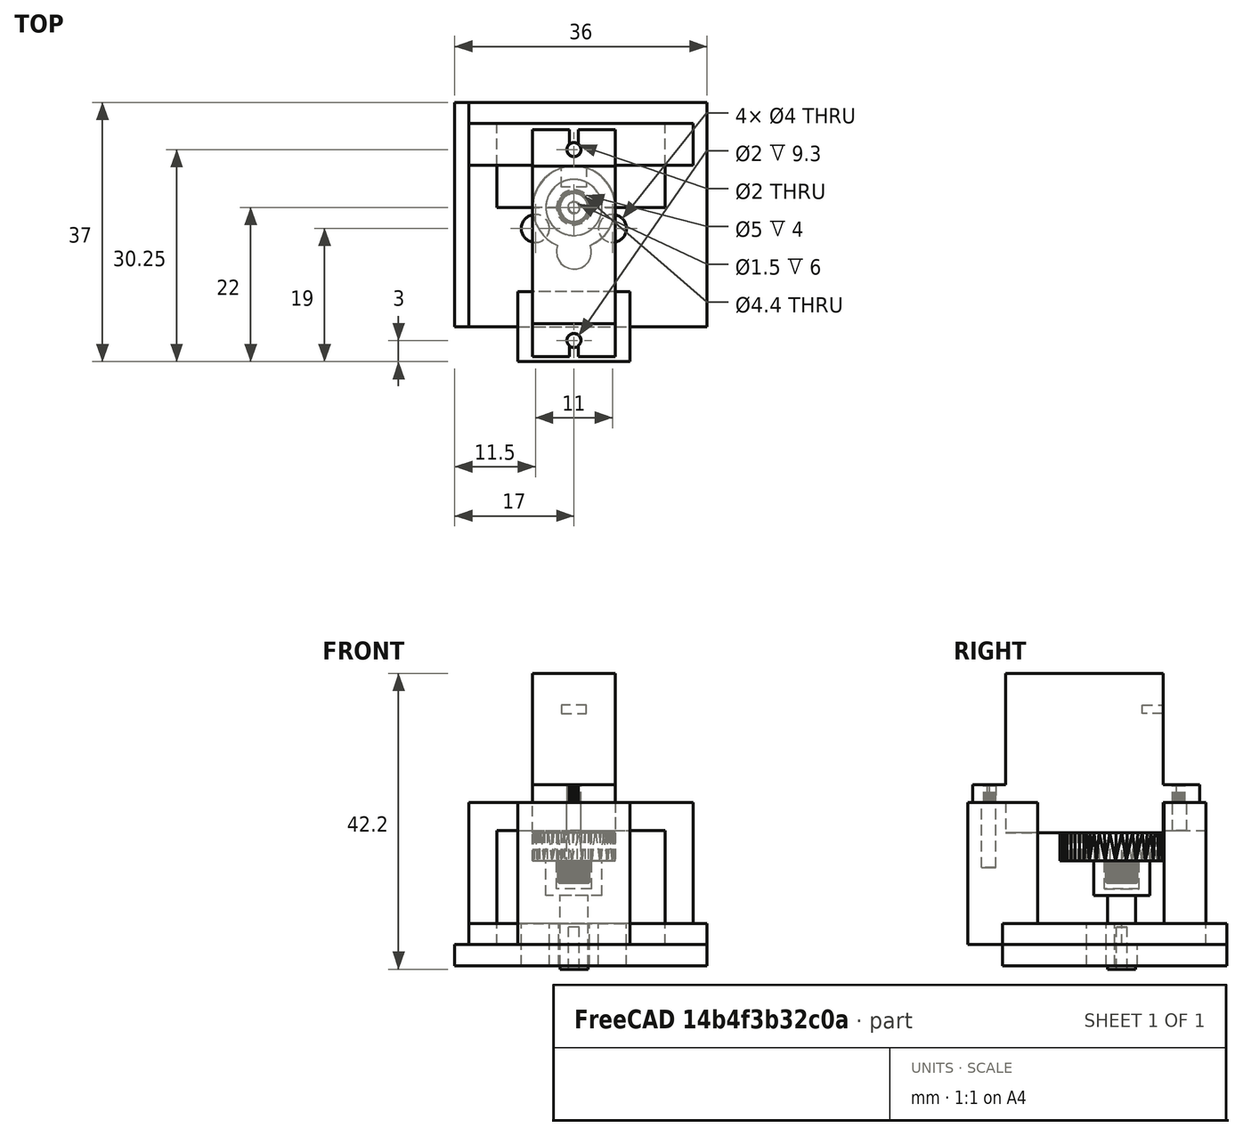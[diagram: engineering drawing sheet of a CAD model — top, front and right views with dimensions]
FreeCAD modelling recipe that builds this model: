
FCSTD DOCUMENT  (FreeCAD 0.17R13541 (Git))
Label: manual valve gauge
License: All rights reserved
LicenseURL: http://en.wikipedia.org/wiki/All_rights_reserved
objects: Part::Cut×13, Part::Cylinder×12, Part::Box×5, Part::Feature×3, Part::MultiFuse×2
note: 35 computed .brp shape members not serialized (recipe doc carries the construction recipe); baked Part::Feature solids carry a one-line shape summary decoded from their .brp

FEATURE [Part::Feature] Servo_SG90001_solid  label="Servo_SG90001 (Solid)"
  Placement = pos=(11,-4.1,23.7) rot=(0.707107,0.707107,0;3.14159rad)
  shape: bbox 11.8 x 32.4 x 29.9 mm, 2326 faces (baked)
FEATURE [Part::Box] Box001  label="Cubo001"
  AttacherType = Attacher::AttachEngine3D
  Height = 3
  Length = 34
  Placement = pos=(2,0,3) rot=(0,0,1;0rad)
  Width = 32
FEATURE [Part::Cylinder] Cylinder003  label="Taladro 004"
  Angle = 360
  AttacherType = Attacher::AttachEngine3D
  Height = 10
  Placement = pos=(11.5,14,0) rot=(0,0,1;0rad)
  Radius = 2
FEATURE [Part::Cylinder] Cylinder004  label="Taladro 005"
  Angle = 360
  AttacherType = Attacher::AttachEngine3D
  Height = 10
  Placement = pos=(22.5,14,0) rot=(0,0,1;0rad)
  Radius = 2
FEATURE [Part::Cylinder] Cylinder005  label="Taladro 006"
  Angle = 360
  AttacherType = Attacher::AttachEngine3D
  Height = 10
  Placement = pos=(17,17,0) rot=(0,0,1;0rad)
  Radius = 2.2
FEATURE [Part::Cut] Cut003
  Base = -> Box001
  Refine = true
  Tool = -> Cylinder003
FEATURE [Part::Cut] Cut004
  Base = -> Cut003
  Refine = true
  Tool = -> Cylinder004
FEATURE [Part::Cut] Cut005  label="Placa servomotor"
  Base = -> Cut004
  Refine = true
  Tool = -> Cylinder005
FEATURE [Part::Box] Box002  label="Soporte 1"
  AttacherType = Attacher::AttachEngine3D
  Height = 20.3
  Length = 16
  Placement = pos=(9,-5,3) rot=(0,0,1;0rad)
  Width = 10
FEATURE [Part::Box] Box003  label="Soporte 002"
  AttacherType = Attacher::AttachEngine3D
  Height = 20.3
  Length = 32
  Placement = pos=(2,23,3) rot=(0,0,1;0rad)
  Width = 6
FEATURE [Part::MultiFuse] Fusion  label="Placa servo con soportes"
  Refine = true
  Shapes = -> [Cut005,Box002,Box003]
FEATURE [Part::Cut] Cut006  label="Placa servo final"
  Base = -> Fusion
  Refine = true
  Tool = -> Servo_SG90001_solid
FEATURE [Part::Box] Box004  label="Cubo002"
  AttacherType = Attacher::AttachEngine3D
  Height = 3
  Length = 36
  Width = 32
FEATURE [Part::Cylinder] Cylinder006  label="Taladro 007"
  Angle = 360
  AttacherType = Attacher::AttachEngine3D
  Height = 10
  Placement = pos=(11.5,14,0) rot=(0,0,1;0rad)
  Radius = 2
FEATURE [Part::Cylinder] Cylinder007  label="Taladro 008"
  Angle = 360
  AttacherType = Attacher::AttachEngine3D
  Height = 10
  Placement = pos=(22.5,14,0) rot=(0,0,1;0rad)
  Radius = 2
FEATURE [Part::Cylinder] Cylinder008  label="Taladro 009"
  Angle = 360
  AttacherType = Attacher::AttachEngine3D
  Height = 10
  Placement = pos=(17,17,0) rot=(0,0,1;0rad)
  Radius = 2.2
FEATURE [Part::Cut] Cut
  Base = -> Box004
  Refine = true
  Tool = -> Cylinder006
FEATURE [Part::Cut] Cut007
  Base = -> Cut
  Refine = true
  Tool = -> Cylinder007
FEATURE [Part::Cut] Cut008  label="Manual valve plate"
  Base = -> Cut007
  Refine = true
  Tool = -> Cylinder008
FEATURE [Part::Feature] Servo_SG90001_solid001  label="Servo_SG90001 (Solid)001"
  Placement = pos=(11,-4.1,23.7) rot=(0.707107,0.707107,0;3.14159rad)
  shape: bbox 11.8 x 32.4 x 29.9 mm, 2326 faces (baked)
FEATURE [Part::Cylinder] Cylinder  label="Taladro 4"
  Angle = 360
  AttacherType = Attacher::AttachEngine3D
  Height = 10
  Placement = pos=(17,-2,14) rot=(0,0,1;0rad)
  Radius = 1
FEATURE [Part::Cylinder] Cylinder009  label="Taladro 5"
  Angle = 360
  AttacherType = Attacher::AttachEngine3D
  Height = 10
  Placement = pos=(17,25.25,14) rot=(0,0,1;0rad)
  Radius = 1
FEATURE [Part::Cut] Cut009
  Base = -> Cut006
  Refine = true
  Tool = -> Cylinder
FEATURE [Part::Cut] Cut010  label="Plataforma servo taladrada"
  Base = -> Cut009
  Refine = true
  Tool = -> Cylinder009
FEATURE [Part::Box] Box005  label="Recorte"
  AttacherType = Attacher::AttachEngine3D
  Height = 16.3
  Length = 24
  Placement = pos=(6,17,3) rot=(0,0,1;0rad)
  Width = 12
FEATURE [Part::Cut] Cut011  label="plataforma servo final"
  Base = -> Cut010
  Refine = true
  Tool = -> Box005
FEATURE [Part::Cylinder] Cylinder010  label="Extensión 1"
  Angle = 360
  AttacherType = Attacher::AttachEngine3D
  Height = 5
  Placement = pos=(17,17,10) rot=(0,0,1;0rad)
  Radius = 4
FEATURE [Part::Cylinder] Cylinder011  label="Extensión 2"
  Angle = 360
  AttacherType = Attacher::AttachEngine3D
  Height = 11.5
  Placement = pos=(17,17,-0.5) rot=(0,0,1;0rad)
  Radius = 2
FEATURE [Part::MultiFuse] Fusion001  label="Extensión"
  Refine = true
  Shapes = -> [Cylinder010,Cylinder011]
FEATURE [Part::Cut] Cut012  label="Extensión final"
  Base = -> Fusion001
  Refine = true
  Tool = -> Servo_SG90001_solid001
FEATURE [Part::Feature] Servo_SG90001_solid002  label="Servo"
  Placement = pos=(11,-4.1,23.7) rot=(0.707107,0.707107,0;3.14159rad)
  shape: bbox 11.8 x 32.4 x 29.9 mm, 2326 faces (baked)
FEATURE [Part::Cylinder] Cylinder012  label="Extensión 003"
  Angle = 360
  AttacherType = Attacher::AttachEngine3D
  Height = 7.5
  Placement = pos=(17,17,-2) rot=(0,0,1;0rad)
  Radius = 0.75
FEATURE [Part::Cut] Cut013  label="Extensión servo"
  Base = -> Cut012
  Refine = true
  Tool = -> Cylinder012
FEATURE [Part::Cylinder] Cylinder013  label="Cilindro"
  Angle = 360
  AttacherType = Attacher::AttachEngine3D
  Height = 4
  Placement = pos=(17,17,11) rot=(0,0,1;0rad)
  Radius = 2.5
FEATURE [Part::Cut] Cut014  label="Extensión servo final"
  Base = -> Cut013
  Refine = true
  Tool = -> Cylinder013
